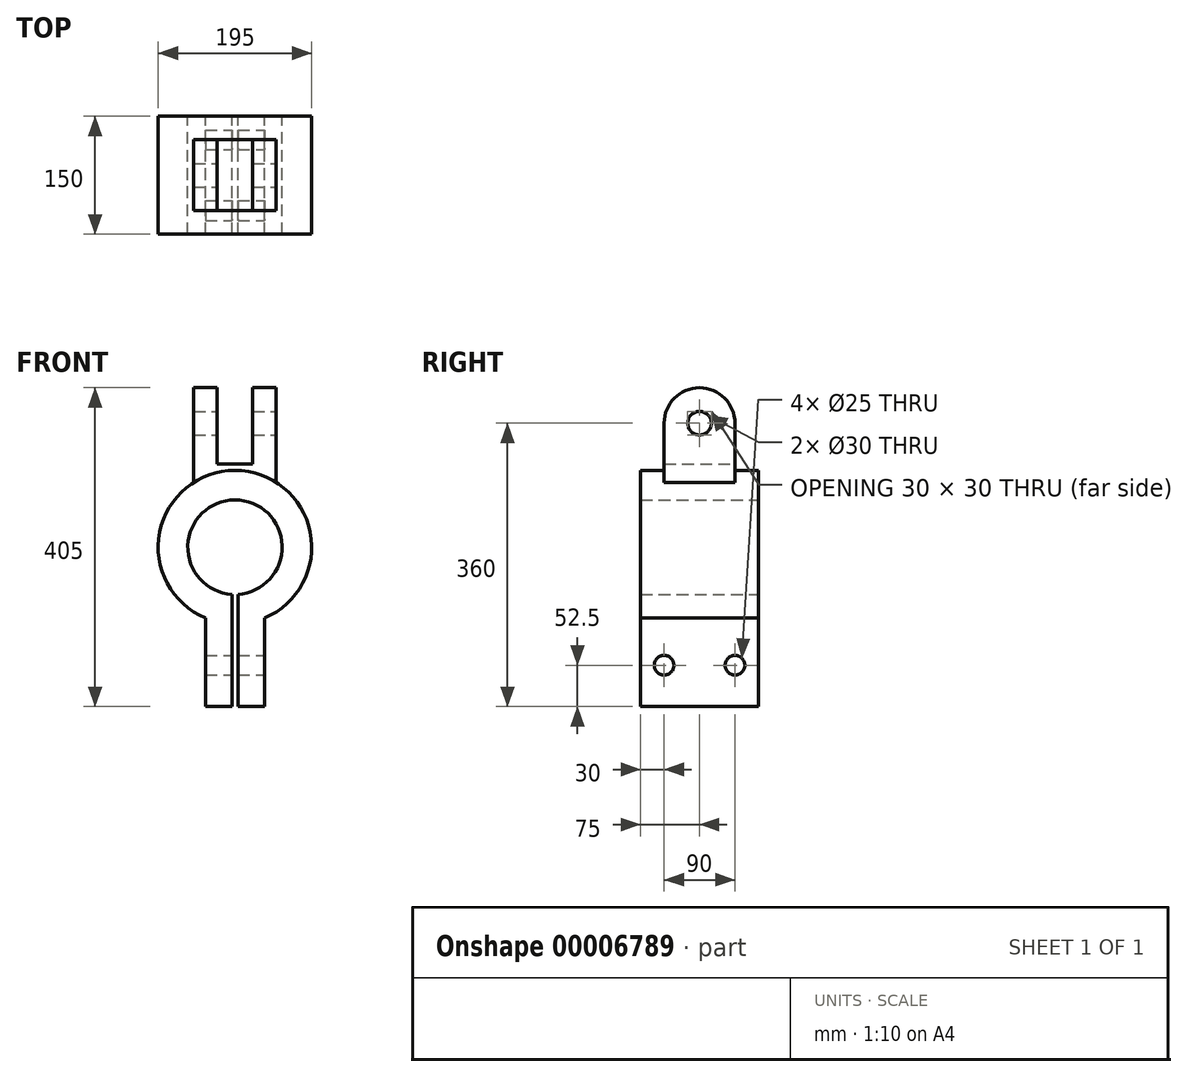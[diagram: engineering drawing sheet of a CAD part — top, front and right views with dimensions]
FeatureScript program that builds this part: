
annotation { "Feature Type Name" : "Feature", "Feature Type Description" : "" }
export const myFeature = defineFeature(function(context is Context, id is Id, definition is map)
    precondition{}
    {
        {
            var Q0;
            Q0=qCreatedBy(makeId("Front.planeOp"),FACE);
            var sketch = newSketch(context, id + "F0", { "sketchPlane" : qUnion([Q0])});
            skArc(sketch, "E0", {"start": v(3.75, -59.88) * mm, "mid": v(0, 60) * mm, "end": v(-3.75, -59.88) * mm});
            skLineSegment(sketch, "E1", {"start": v(-3.75, -59.88) * mm, "end": v(-3.75, -202.5) * mm});
            skLineSegment(sketch, "E2", {"start": v(-3.75, -202.5) * mm, "end": v(-37.5, -202.5) * mm});
            skLineSegment(sketch, "E3", {"start": v(-37.5, -202.5) * mm, "end": v(-37.5, -90) * mm});
            skLineSegment(sketch, "E4", {"start": v(0, 0) * mm, "end": v(0, -202.5) * mm, "construction": true});
            skLineSegment(sketch, "E5.0.MirrorCS", {"start": v(3.75, -59.88) * mm, "end": v(3.75, -202.5) * mm});
            skLineSegment(sketch, "E5.1.MirrorCS", {"start": v(37.5, -202.5) * mm, "end": v(37.5, -90) * mm});
            skLineSegment(sketch, "E5.2.MirrorCS", {"start": v(3.75, -202.5) * mm, "end": v(37.5, -202.5) * mm});
            skArc(sketch, "E6.trimOffspring", {"start": v(37.5, -90) * mm, "mid": v(0, 97.5) * mm, "end": v(-37.5, -90) * mm});
            skSolve(sketch);
        }
        {
            var Q0;
            Q0 = qSketchRegion(id + "F0", true);
            extrude(context, id + "F1", {"entities" : qUnion([Q0]), "endBound" : BoundingType.SYMMETRIC, "depth" : 150 * mm});
        }
        {
            var Q0;
            Q0=qCreatedBy(makeId("Front.planeOp"),FACE);
            var sketch = newSketch(context, id + "F2", { "sketchPlane" : qUnion([Q0])});
            skLineSegment(sketch, "E7.bottom", {"start": v(-52.5, 75) * mm, "end": v(52.5, 75) * mm});
            skLineSegment(sketch, "E7.left", {"start": v(-52.5, 75) * mm, "end": v(-52.5, 202.5) * mm});
            skLineSegment(sketch, "E7.right", {"start": v(52.5, 75) * mm, "end": v(52.5, 202.5) * mm});
            skLineSegment(sketch, "E8", {"start": v(-52.5, 202.5) * mm, "end": v(-22.5, 202.5) * mm});
            skLineSegment(sketch, "E9", {"start": v(-22.5, 202.5) * mm, "end": v(-22.5, 105.5) * mm});
            skLineSegment(sketch, "E10", {"start": v(-22.5, 105.5) * mm, "end": v(22.5, 105.5) * mm});
            skLineSegment(sketch, "E11", {"start": v(22.5, 105.5) * mm, "end": v(22.5, 202.5) * mm});
            skLineSegment(sketch, "E12", {"start": v(22.5, 202.5) * mm, "end": v(52.5, 202.5) * mm});
            skSolve(sketch);
        }
        {
            var Q0;
            Q0 = qSketchRegion(id + "F2", true);
            extrude(context, id + "F3", {"entities" : qUnion([Q0]), "operationType" : NewBodyOperationType.ADD, "endBound" : BoundingType.SYMMETRIC, "depth" : 90 * mm});
        }
        {
            var Q0;
            Q0=makeQuery(id+"F3.opExtrude","CAP_EDGE",EDGE,{"disambiguationData":[OSD([sQuery(id+"F2.wireOp",EDGE,"E12")])],"isStart":false});
            var Q1;
            Q1=makeQuery(id+"F3.opExtrude","CAP_EDGE",EDGE,{"disambiguationData":[OSD([sQuery(id+"F2.wireOp",EDGE,"E12")])],"isStart":true});
            var Q2;
            Q2=makeQuery(id+"F3.opExtrude","CAP_EDGE",EDGE,{"disambiguationData":[OSD([sQuery(id+"F2.wireOp",EDGE,"E8")])],"isStart":false});
            var Q3;
            Q3=makeQuery(id+"F3.opExtrude","CAP_EDGE",EDGE,{"disambiguationData":[OSD([sQuery(id+"F2.wireOp",EDGE,"E8")])],"isStart":true});
            fillet(context, id + "F4", {"entities" : qUnion([Q0, Q1, Q2, Q3]), "radius" : 45 * mm, "tangentPropagation" : true, "allowEdgeOverflow" : false});
        }
        {
            var Q0;
            Q0=makeQuery(id+"F3.opExtrude","SWEPT_FACE",FACE,{"disambiguationData":[OSD([sQuery(id+"F2.wireOp",EDGE,"E7.right")])]});
            var sketch = newSketch(context, id + "F5", { "sketchPlane" : qUnion([Q0])});
            skCircle(sketch, "E13", {"center": v(0, 157.5) * mm, "radius": 15 * mm});
            skSolve(sketch);
        }
        {
            var Q0;
            Q0 = qSketchRegion(id + "F5", true);
            extrude(context, id + "F6", {"entities" : qUnion([Q0]), "operationType" : NewBodyOperationType.REMOVE, "endBound" : BoundingType.THROUGH_ALL, "oppositeDirection" : true, "depth" : 25 * mm});
        }
        {
            var Q0;
            Q0=makeQuery(id+"F1.opExtrude","SWEPT_FACE",FACE,{"disambiguationData":[OSD([sQuery(id+"F0.wireOp",EDGE,"E5.1.MirrorCS")])]});
            var sketch = newSketch(context, id + "F7", { "sketchPlane" : qUnion([Q0])});
            skCircle(sketch, "E14", {"center": v(-45, -150) * mm, "radius": 12.5 * mm});
            skCircle(sketch, "E15", {"center": v(45, -150) * mm, "radius": 12.5 * mm});
            skSolve(sketch);
        }
        {
            var Q0;
            Q0 = qSketchRegion(id + "F7", true);
            extrude(context, id + "F8", {"entities" : qUnion([Q0]), "operationType" : NewBodyOperationType.REMOVE, "endBound" : BoundingType.THROUGH_ALL, "oppositeDirection" : true, "depth" : 25 * mm});
        }
    });
